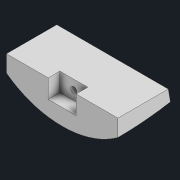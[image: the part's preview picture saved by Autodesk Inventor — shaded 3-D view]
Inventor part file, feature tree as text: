
AUTODESK INVENTOR PART (.ipt)
format: ipt  version: 2022 (Build 260153000, 153)  size: 125,952 bytes
history: native  units: mm
features: sketch x5, extrude x3, revolve x1, hole x1, projected_geometry x1
ambient origin geometry x8: Origin, YZ Plane, XZ Plane, XY Plane, X Axis, Y Axis, Z Axis, Center Point
bodies: Body1 (feature_tree)
feature tree (11):
  revolve  "回転2"
  extrude  "押し出し1"  Depth=120.0mm
  extrude  "押し出し2"  Depth=18.0mm
  extrude  "押し出し3"  Depth=37.5mm
  hole  "穴1"  [1 undecoded]
  sketch  "スケッチ2"
  sketch  "スケッチ3"
  sketch  "スケッチ5"
  projected_geometry  "投影ループ1"
  sketch  "スケッチ7"
  sketch  "スケッチ8"
note: 1 required parameter value undecoded (feature->parameter linkage not recoverable at this tier; creation-order binding heuristic only, values carry confidence <= 0.55)
